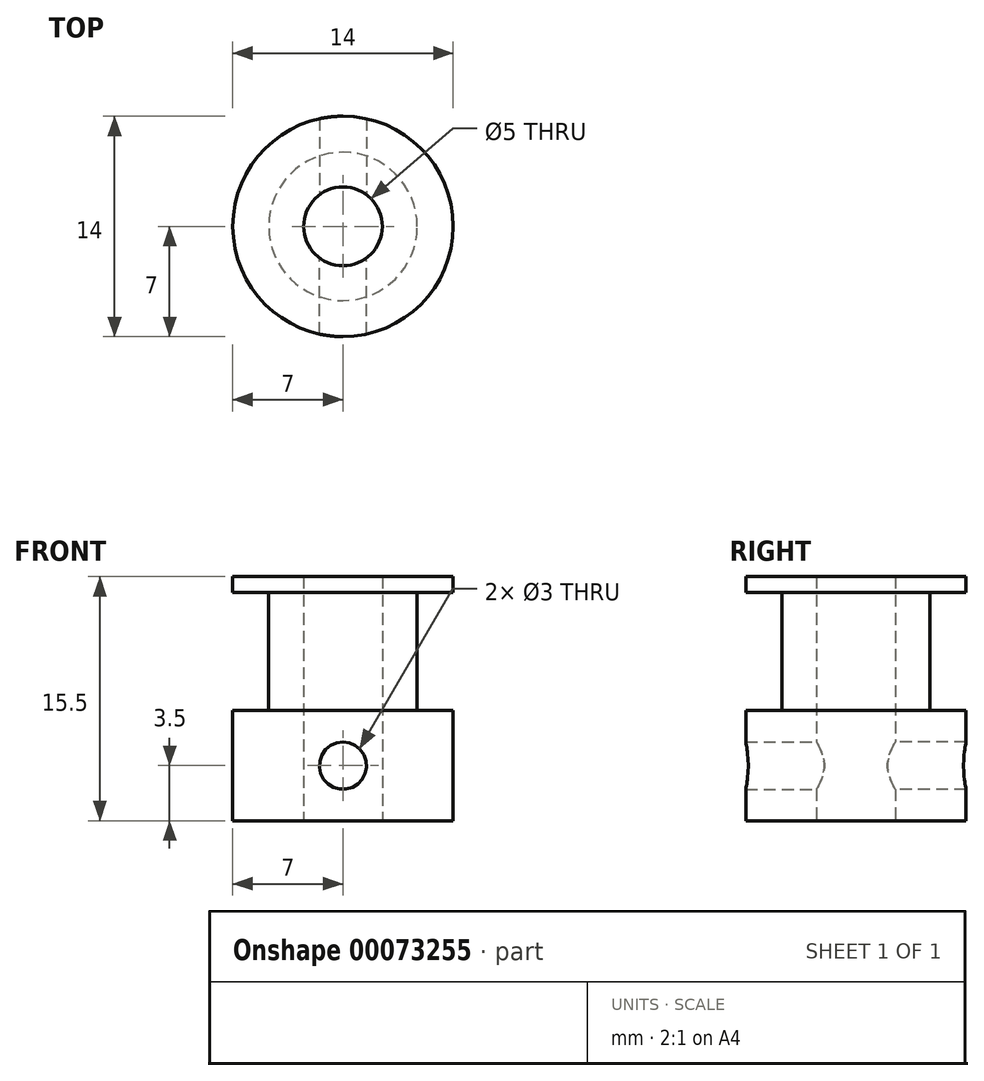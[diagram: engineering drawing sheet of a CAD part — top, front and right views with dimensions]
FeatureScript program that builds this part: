
annotation { "Feature Type Name" : "Feature", "Feature Type Description" : "" }
export const myFeature = defineFeature(function(context is Context, id is Id, definition is map)
    precondition{}
    {
        {
            var Q0;
            Q0=qCreatedBy(makeId("Front.planeOp"),FACE);
            var sketch = newSketch(context, id + "F0", { "sketchPlane" : qUnion([Q0])});
            skLineSegment(sketch, "E0", {"start": v(0, 0) * mm, "end": v(14, 0) * mm});
            skLineSegment(sketch, "E1", {"start": v(14, 0) * mm, "end": v(14, 7) * mm});
            skLineSegment(sketch, "E2", {"start": v(14, 14.5) * mm, "end": v(14, 15.5) * mm});
            skLineSegment(sketch, "E3", {"start": v(14, 15.5) * mm, "end": v(0, 15.5) * mm});
            skLineSegment(sketch, "E4", {"start": v(0, 15.5) * mm, "end": v(0, 14.5) * mm});
            skLineSegment(sketch, "E5", {"start": v(0, 14.5) * mm, "end": v(2.29, 14.5) * mm});
            skLineSegment(sketch, "E6", {"start": v(2.29, 14.5) * mm, "end": v(2.29, 7) * mm});
            skLineSegment(sketch, "E7", {"start": v(2.29, 7) * mm, "end": v(0, 7) * mm});
            skLineSegment(sketch, "E8", {"start": v(0, 7) * mm, "end": v(0, 0) * mm});
            skLineSegment(sketch, "E9", {"start": v(7, 0) * mm, "end": v(7, 15.5) * mm});
            skPoint(sketch, "E10", {"position": v(4.5, 0) * mm});
            skPoint(sketch, "E11", {"position": v(9.5, 0) * mm});
            skLineSegment(sketch, "E12", {"start": v(4.5, 0) * mm, "end": v(4.5, 15.5) * mm});
            skLineSegment(sketch, "E13", {"start": v(9.5, 0) * mm, "end": v(9.5, 15.5) * mm});
            skLineSegment(sketch, "E14", {"start": v(14, 7) * mm, "end": v(11.71, 7) * mm});
            skLineSegment(sketch, "E15", {"start": v(11.71, 7) * mm, "end": v(11.71, 14.5) * mm});
            skLineSegment(sketch, "E16", {"start": v(11.71, 14.5) * mm, "end": v(14, 14.5) * mm});
            skSolve(sketch);
        }
        {
            var Q0;
            {var subQ0=sQuery(id+"F0.wireOp",EDGE,"E4");Q0=makeQuery(id+"F0.imprint","IMPRINT",FACE,{"disambiguationData":[TD([[makeQuery(id+"F0.imprint","IMPRINT",EDGE,{"derivedFrom":subQ0}),1.0]])]});}
            var Q1;
            Q1=sQuery(id+"F0.wireOp",EDGE,"E9");
            revolve(context, id + "F1", {"entities" : qUnion([Q0]), "axis" : qUnion([Q1]), "revolveType" : RevolveType.FULL});
        }
        {
            var Q0;
            Q0=qCreatedBy(makeId("Front.planeOp"),FACE);
            var sketch = newSketch(context, id + "F2", { "sketchPlane" : qUnion([Q0])});
            skLineSegment(sketch, "E17", {"start": v(0, 0) * mm, "end": v(7, 0) * mm});
            skLineSegment(sketch, "E18", {"start": v(7, 0) * mm, "end": v(7, 7) * mm});
            skCircle(sketch, "E19", {"center": v(7, 3.5) * mm, "radius": 1.5 * mm});
            skSolve(sketch);
        }
        {
            var Q0;
            {var subQ0=sQuery(id+"F2.wireOp",EDGE,"E19");var subQ1=sQuery(id+"F2.wireOp",EDGE,"E18");var subQ2=makeQuery(id+"F2.imprint","INTERSECT",VERTEX,{"disambiguationData":[OD(0.0)],"derivedFrom":[subQ1,subQ0]});Q0=makeQuery(id+"F2.imprint","IMPRINT",FACE,{"disambiguationData":[TD([[makeQuery(id+"F2.imprint","IMPRINT",EDGE,{"disambiguationData":[TD([[subQ2,-1.0]])],"derivedFrom":subQ1}),-1.0]])]});}
            var Q1;
            {var subQ0=sQuery(id+"F2.wireOp",EDGE,"E19");var subQ1=sQuery(id+"F2.wireOp",EDGE,"E18");var subQ2=makeQuery(id+"F2.imprint","INTERSECT",VERTEX,{"disambiguationData":[OD(0.0)],"derivedFrom":[subQ1,subQ0]});Q1=makeQuery(id+"F2.imprint","IMPRINT",FACE,{"disambiguationData":[TD([[makeQuery(id+"F2.imprint","IMPRINT",EDGE,{"disambiguationData":[TD([[subQ2,-1.0]])],"derivedFrom":subQ1}),1.0]])]});}
            extrude(context, id + "F3", {"entities" : qUnion([Q0, Q1]), "operationType" : NewBodyOperationType.REMOVE, "endBound" : BoundingType.THROUGH_ALL, "oppositeDirection" : true, "depth" : 25.4 * mm});
        }
        {
            var Q0;
            {var subQ0=sQuery(id+"F2.wireOp",EDGE,"E19");var subQ1=sQuery(id+"F2.wireOp",EDGE,"E18");var subQ2=makeQuery(id+"F2.imprint","INTERSECT",VERTEX,{"disambiguationData":[OD(0.0)],"derivedFrom":[subQ1,subQ0]});Q0=makeQuery(id+"F2.imprint","IMPRINT",FACE,{"disambiguationData":[TD([[makeQuery(id+"F2.imprint","IMPRINT",EDGE,{"disambiguationData":[TD([[subQ2,-1.0]])],"derivedFrom":subQ1}),1.0]])]});}
            var Q1;
            {var subQ0=sQuery(id+"F2.wireOp",EDGE,"E19");var subQ1=sQuery(id+"F2.wireOp",EDGE,"E18");var subQ2=makeQuery(id+"F2.imprint","INTERSECT",VERTEX,{"disambiguationData":[OD(0.0)],"derivedFrom":[subQ1,subQ0]});Q1=makeQuery(id+"F2.imprint","IMPRINT",FACE,{"disambiguationData":[TD([[makeQuery(id+"F2.imprint","IMPRINT",EDGE,{"disambiguationData":[TD([[subQ2,-1.0]])],"derivedFrom":subQ1}),-1.0]])]});}
            extrude(context, id + "F4", {"entities" : qUnion([Q0, Q1]), "operationType" : NewBodyOperationType.REMOVE, "depth" : 25.4 * mm});
        }
    });
